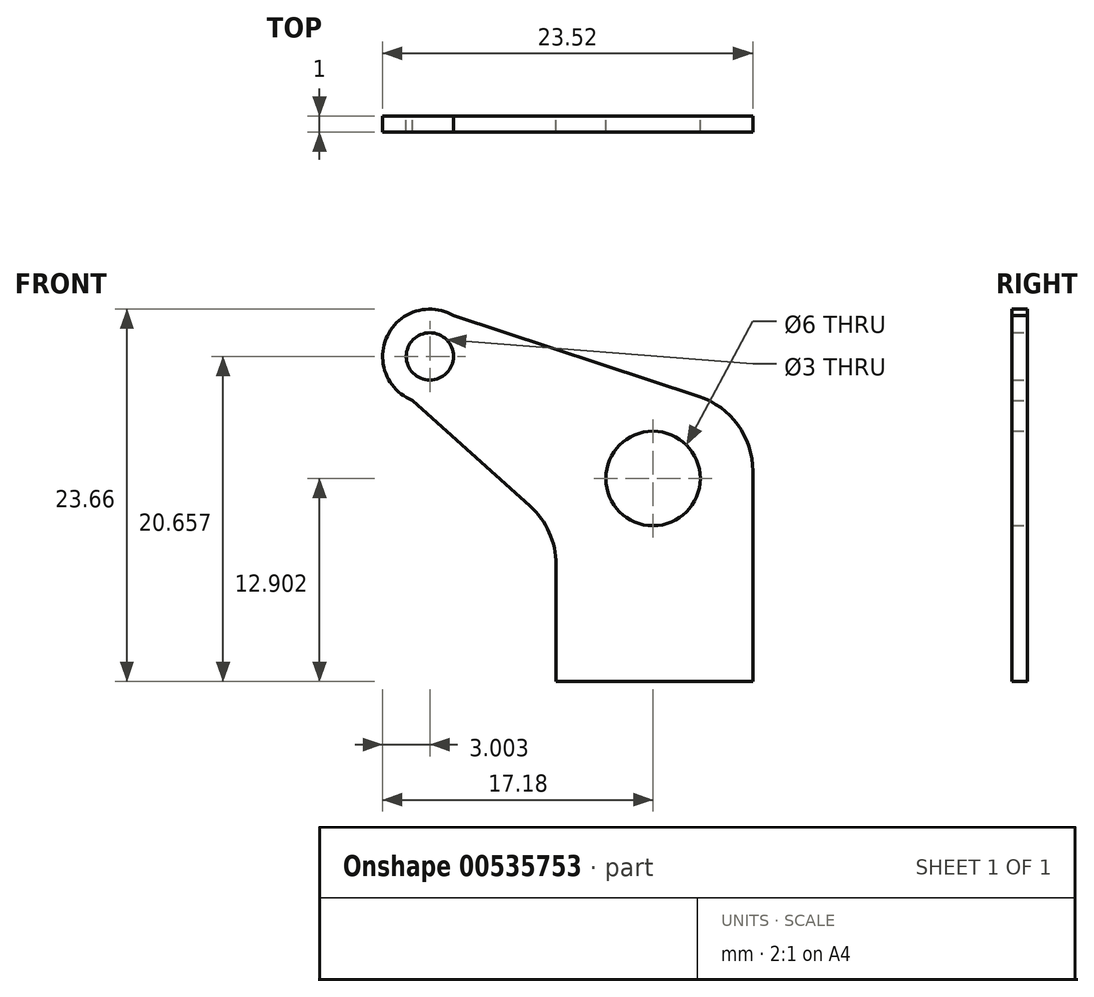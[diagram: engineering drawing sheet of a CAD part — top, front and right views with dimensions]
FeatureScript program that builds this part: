
annotation { "Feature Type Name" : "Feature", "Feature Type Description" : "" }
export const myFeature = defineFeature(function(context is Context, id is Id, definition is map)
    precondition{}
    {
        {
            var Q0;
            Q0=qCreatedBy(makeId("Front.planeOp"),FACE);
            var sketch = newSketch(context, id + "F0", { "sketchPlane" : qUnion([Q0])});
            skCircle(sketch, "E0", {"center": v(-43.86, -5.18) * mm, "radius": 1.5 * mm});
            skArc(sketch, "E1", {"start": v(-42.36, -2.58) * mm, "mid": v(-46.56, -3.88) * mm, "end": v(-44.97, -7.97) * mm});
            skCircle(sketch, "E2", {"center": v(-29.68, -12.94) * mm, "radius": 3 * mm});
            skLineSegment(sketch, "E3", {"start": v(-43.52, -2.2) * mm, "end": v(-26.78, -7.72) * mm});
            skLineSegment(sketch, "E4", {"start": v(-44.97, -7.97) * mm, "end": v(-37.5, -14.68) * mm});
            skLineSegment(sketch, "E5", {"start": v(-35.84, -25.84) * mm, "end": v(-23.34, -25.84) * mm});
            skLineSegment(sketch, "E6", {"start": v(-23.34, -25.84) * mm, "end": v(-23.34, -12.47) * mm});
            skLineSegment(sketch, "E7", {"start": v(-35.84, -25.84) * mm, "end": v(-35.84, -18.4) * mm});
            skPoint(sketch, "E8.visualSharp", {"position": v(-23.34, -8.85) * mm});
            skArc(sketch, "E8.filletArc", {"start": v(-23.34, -12.47) * mm, "mid": v(-24.3, -9.54) * mm, "end": v(-26.78, -7.72) * mm});
            skPoint(sketch, "E9.visualSharp", {"position": v(-35.84, -16.17) * mm});
            skArc(sketch, "E9.filletArc", {"start": v(-35.84, -18.4) * mm, "mid": v(-36.28, -16.37) * mm, "end": v(-37.5, -14.68) * mm});
            skSolve(sketch);
        }
        {
            var Q0;
            Q0 = qSketchRegion(id + "F0", true);
            extrude(context, id + "F1", {"entities" : qUnion([Q0]), "endBound" : BoundingType.SYMMETRIC, "depth" : 1 * mm, "offsetDistance" : 25 * mm});
        }
    });
